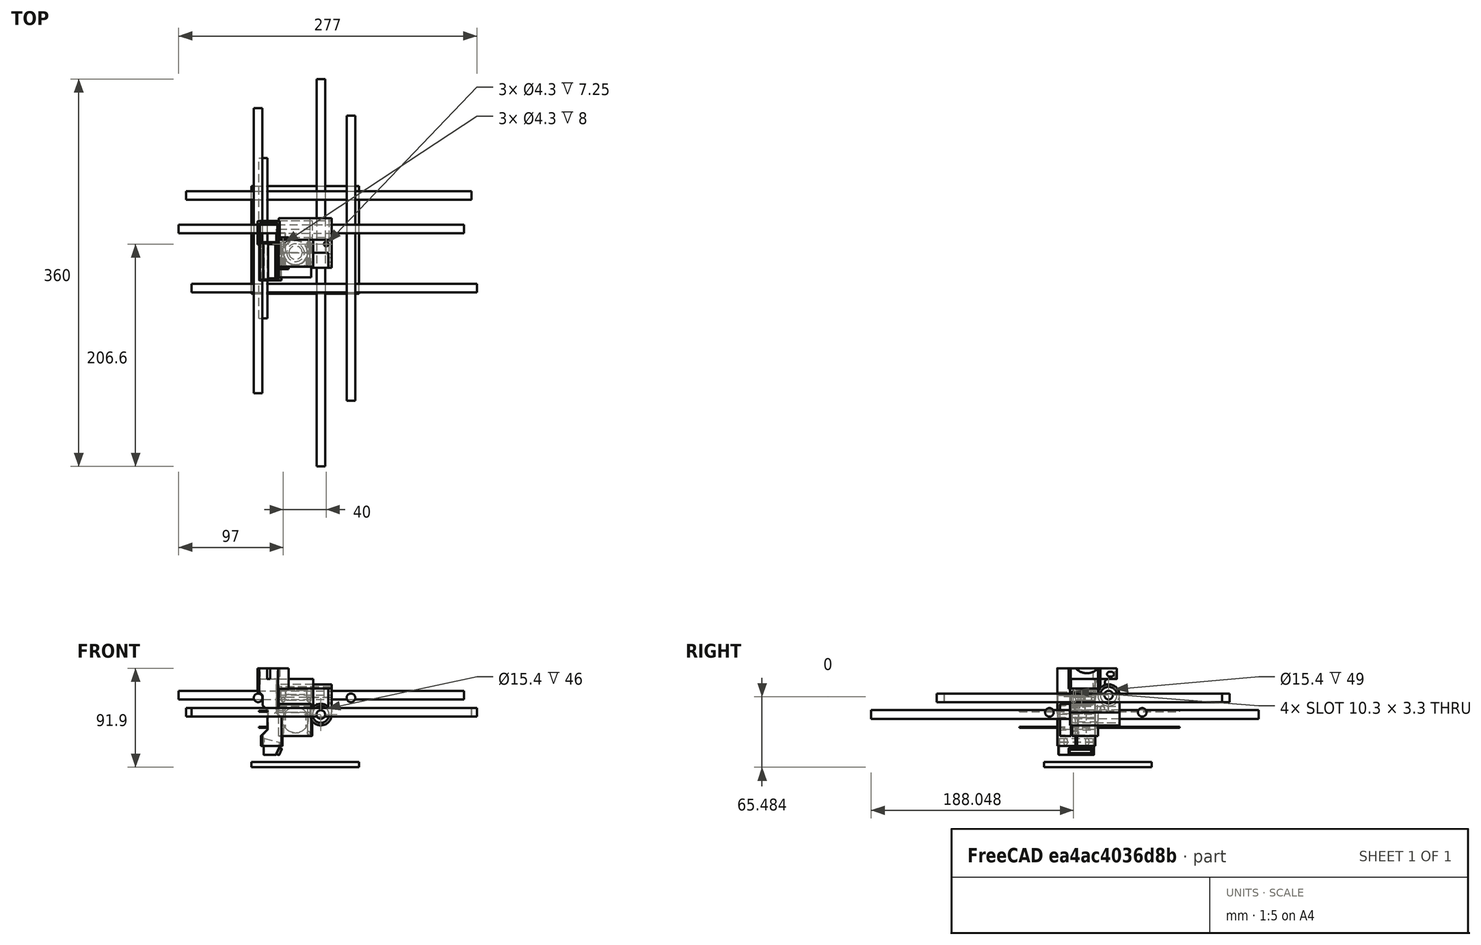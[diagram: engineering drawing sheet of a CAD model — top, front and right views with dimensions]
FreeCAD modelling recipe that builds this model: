
FCSTD DOCUMENT  (FreeCAD 0.17R)
Label: Carrier_E3DV6
License: All rights reserved
LicenseURL: http://en.wikipedia.org/wiki/All_rights_reserved
objects: Sketcher::SketchObject×28, App::DocumentObjectGroup×23, PartDesign::Pocket×21, PartDesign::FeatureBase×17, PartDesign::Body×7, PartDesign::Pad×6, Part::Box×6, Part::Cylinder×6, PartDesign::Fillet×5, Part::Feature×4, PartDesign::Line×3, Part::Cut×2, PartDesign::Revolution×1, App::Part×1, Mesh::Feature×1
note: 134 computed .brp shape members not serialized (recipe doc carries the construction recipe); baked Part::Feature solids carry a one-line shape summary decoded from their .brp

FEATURE [Sketcher::SketchObject] Sketch
  MapMode = 5
  Support = -> [XY_Plane]
  sketch-geometry (4):
    g0: LineSegment StartX=-15.5 StartY=12 StartZ=0 EndX=15.5 EndY=12 EndZ=0
    g1: LineSegment StartX=15.5 StartY=12 StartZ=0 EndX=15.5 EndY=-12 EndZ=0
    g2: LineSegment StartX=15.5 StartY=-12 StartZ=0 EndX=-15.5 EndY=-12 EndZ=0
    g3: LineSegment StartX=-15.5 StartY=-12 StartZ=0 EndX=-15.5 EndY=12 EndZ=0
  constraints (12):
    c: Coincident(g0,g1)
    c: Coincident(g1,g2)
    c: Coincident(g2,g3)
    c: Coincident(g3,g0)
    c: Horizontal(g0)
    c: Horizontal(g2)
    c: Vertical(g1)
    c: Vertical(g3)
    c: Symmetric(g0,g0,g-2)
    c: Symmetric(g0,g1,g-1)
    c: DistanceX(g0,g0) = 31
    c: DistanceY(g3,g3) = 24
FEATURE [PartDesign::Pad] Pad  label="FS_BaseBody"
  Length = 22
  Length2 = 100
  Profile = -> Sketch
  Type = 0
FEATURE [Sketcher::SketchObject] Sketch001
  ExternalGeometry = -> [Pad]
  MapMode = 5
  Placement = pos=(0,-12,0) rot=(1,0,0;1.5708rad)
  Support = -> [Pad]
  sketch-geometry (6):
    g0: LineSegment [constr] StartX=0 StartY=15 StartZ=0 EndX=-15.5 EndY=15 EndZ=0
    g1: Circle CenterX=0 CenterY=15 CenterZ=0 NormalX=0 NormalY=0 NormalZ=1 AngleXU=0 Radius=12
    g2: Circle CenterX=-12 CenterY=3 CenterZ=0 NormalX=0 NormalY=0 NormalZ=1 AngleXU=0 Radius=1.3
    g3: Circle CenterX=12 CenterY=3 CenterZ=0 NormalX=0 NormalY=0 NormalZ=1 AngleXU=0 Radius=1.3
    g4: Circle CenterX=12 CenterY=27 CenterZ=0 NormalX=0 NormalY=0 NormalZ=1 AngleXU=0 Radius=1.3
    g5: Circle CenterX=-12 CenterY=27 CenterZ=0 NormalX=0 NormalY=0 NormalZ=1 AngleXU=0 Radius=1.3
  constraints (16):
    c: PointOnObject(g0,g-2)
    c: PointOnObject(g0,g-3)
    c: Horizontal(g0)
    c: DistanceY(g-6,g0) = 15
    c: Coincident(g1,g0)
    c: Radius(g1) = 12
    c: Symmetric(g2,g3,g-2)
    c: Symmetric(g5,g4,g-2)
    c: Distance(g2,g3) = 24
    c: DistanceX(g5,g4) = 24
    c: Distance(g5,g2) = 24
    c: DistanceY(g-6,g2) = 3
    c: Radius(g5) = 1.3
    c: Equal(g5,g4)
    c: Equal(g5,g3)
    c: Equal(g5,g2)
FEATURE [PartDesign::Pocket] Pocket  label="FS_FanCutout_Pocket"
  BaseFeature = -> Pad
  Length = 6
  Length2 = 100
  Profile = -> Sketch001
  Type = 0
FEATURE [Sketcher::SketchObject] Sketch002
  MapMode = 5
  Placement = pos=(0,0,0) rot=(1,0,0;3.14159rad)
  Support = -> [Pocket]
  sketch-geometry (1):
    g0: Circle CenterX=0 CenterY=0 CenterZ=0 NormalX=0 NormalY=0 NormalZ=1 AngleXU=0 Radius=11.25
  constraints (3):
    c: PointOnObject(g0,g-1)
    c: Coincident(g0,g-1)
    c: Radius(g0) = 11.25
FEATURE [PartDesign::Pocket] Pocket001  label="FS_EDV6_Cutout_Pocket"
  BaseFeature = -> Pocket
  Length = 5
  Length2 = 100
  Profile = -> Sketch002
  Type = 1
FEATURE [Sketcher::SketchObject] Sketch003
  ExternalGeometry = -> [Pocket001]
  MapMode = 5
  Placement = pos=(0,12,0) rot=(0,0.707107,0.707107;3.14159rad)
  Support = -> [Pocket001]
  sketch-geometry (4):
    g0: LineSegment StartX=-11.25 StartY=22 StartZ=0 EndX=11.25 EndY=22 EndZ=0
    g1: LineSegment StartX=11.25 StartY=22 StartZ=0 EndX=11.25 EndY=0 EndZ=0
    g2: LineSegment StartX=11.25 StartY=0 StartZ=0 EndX=-11.25 EndY=0 EndZ=0
    g3: LineSegment StartX=-11.25 StartY=0 StartZ=0 EndX=-11.25 EndY=22 EndZ=0
  constraints (12):
    c: Coincident(g0,g1)
    c: Coincident(g1,g2)
    c: Coincident(g2,g3)
    c: Coincident(g3,g0)
    c: Horizontal(g0)
    c: Horizontal(g2)
    c: Vertical(g1)
    c: Vertical(g3)
    c: Symmetric(g1,g2,g-2)
    c: DistanceX(g0,g0) = 22.5
    c: PointOnObject(g2,g-1)
    c: PointOnObject(g0,g-3)
FEATURE [PartDesign::Pocket] Pocket002  label="FS_EDV6_Cutout_Back"
  BaseFeature = -> Pocket001
  Length = 11
  Length2 = 100
  Profile = -> Sketch003
  Type = 0
FEATURE [Sketcher::SketchObject] Sketch004
  ExternalGeometry = -> [Pocket002]
  MapMode = 5
  Placement = pos=(0,-12,0) rot=(1,0,0;1.5708rad)
  Support = -> [Pocket002]
  sketch-geometry (1):
    g0: Circle CenterX=23.47 CenterY=19.93 CenterZ=0 NormalX=0 NormalY=0 NormalZ=1 AngleXU=0 Radius=10.5
  constraints (3):
    c: Radius(g0) = 10.5
    c: DistanceY(g-1,g0) = 19.93
    c: DistanceX(g-1,g0) = 23.47
FEATURE [PartDesign::Pocket] Pocket003  label="FS_Cutout_Axis_Pocket"
  BaseFeature = -> Pocket002
  Length = 5
  Length2 = 100
  Profile = -> Sketch004
  Type = 1
FEATURE [Sketcher::SketchObject] Sketch005
  MapMode = 5
  Placement = pos=(0,0,0) rot=(1,0,0;1.5708rad)
  Support = -> [XZ_Plane001]
  sketch-geometry (4):
    g0: LineSegment StartX=-24.5 StartY=11 StartZ=0 EndX=24.5 EndY=11 EndZ=0
    g1: LineSegment StartX=24.5 StartY=11 StartZ=0 EndX=24.5 EndY=-11 EndZ=0
    g2: LineSegment StartX=24.5 StartY=-11 StartZ=0 EndX=-24.5 EndY=-11 EndZ=0
    g3: LineSegment StartX=-24.5 StartY=-11 StartZ=0 EndX=-24.5 EndY=11 EndZ=0
  constraints (12):
    c: Coincident(g0,g1)
    c: Coincident(g1,g2)
    c: Coincident(g2,g3)
    c: Coincident(g3,g0)
    c: Horizontal(g0)
    c: Horizontal(g2)
    c: Vertical(g1)
    c: Vertical(g3)
    c: DistanceX(g2,g2) = 49
    c: DistanceY(g1,g1) = 22
    c: Symmetric(g1,g2,g-2)
    c: Symmetric(g0,g1,g-1)
FEATURE [PartDesign::Pad] Pad001  label="HET1_Base_Pad"
  Length = 12
  Length2 = 100
  Placement = pos=(0,0,0) rot=(1,0,0;1.5708rad)
  Profile = -> Sketch005
  Type = 0
FEATURE [Sketcher::SketchObject] Sketch006  label="HET1_Holes_Top"
  ExternalGeometry = -> [Pad001]
  MapMode = 5
  Placement = pos=(0,-1e-12,11) rot=(0,0,1;3.14159rad)
  Support = -> [Pad001]
  sketch-geometry (4):
    g0: Circle CenterX=20.5 CenterY=4 CenterZ=0 NormalX=0 NormalY=0 NormalZ=1 AngleXU=0 Radius=2.15
    g1: Circle CenterX=-19.5 CenterY=4 CenterZ=0 NormalX=0 NormalY=0 NormalZ=1 AngleXU=0 Radius=2.15
    g2: LineSegment [constr] StartX=-19.5 StartY=4 StartZ=0 EndX=20.5 EndY=4 EndZ=0
    g3: Circle CenterX=-3.5 CenterY=4 CenterZ=0 NormalX=0 NormalY=0 NormalZ=1 AngleXU=0 Radius=2.15
  constraints (11):
    c: DistanceX(g1,g0) = 40
    c: Radius(g1) = 2.15
    c: Equal(g1,g0)
    c: DistanceX(g0,g-3) = 4
    c: DistanceY(g-3,g0) = 4
    c: Coincident(g2,g1)
    c: Coincident(g2,g0)
    c: Horizontal(g2)
    c: PointOnObject(g3,g2)
    c: Radius(g3) = 2.15
    c: DistanceX(g3,g0) = 24
FEATURE [PartDesign::Pocket] Pocket004  label="HET1_Holes_Top_Pocket"
  BaseFeature = -> Pad001
  Length = 8
  Length2 = 100
  Placement = pos=(0,0,0) rot=(1,0,0;1.5708rad)
  Profile = -> Sketch006
  Type = 0
FEATURE [Sketcher::SketchObject] Sketch007
  ExternalGeometry = -> [Pocket004]
  MapMode = 5
  Placement = pos=(0,-12,-1e-12) rot=(1,0,0;1.5708rad)
  Support = -> [Pocket004]
  sketch-geometry (2):
    g0: Circle CenterX=-20.5 CenterY=1 CenterZ=0 NormalX=0 NormalY=0 NormalZ=1 AngleXU=0 Radius=2.15
    g1: Circle CenterX=3.5 CenterY=1 CenterZ=0 NormalX=0 NormalY=0 NormalZ=1 AngleXU=0 Radius=2.15
  constraints (6):
    c: Radius(g0) = 2.15
    c: Equal(g0,g1)
    c: DistanceX(g0,g1) = 24
    c: DistanceX(g-3,g0) = 4
    c: DistanceY(g-3,g0) = 12
    c: DistanceY(g-3,g1) = 12
FEATURE [PartDesign::Pocket] Pocket005  label="HET1_Holes_Front_Pocket"
  BaseFeature = -> Pocket004
  Length = 6
  Length2 = 100
  Placement = pos=(0,0,0) rot=(1,0,0;1.5708rad)
  Profile = -> Sketch007
  Type = 0
FEATURE [Sketcher::SketchObject] Sketch008
  ExternalGeometry = -> [Pocket004]
  MapMode = 5
  Placement = pos=(0,0,-11) rot=(1,0,0;3.14159rad)
  Support = -> [Pocket005]
  sketch-geometry (6):
    g0: LineSegment StartX=-24.5 StartY=0 StartZ=0 EndX=-24.5 EndY=-9.75 EndZ=0
    g1: LineSegment StartX=-24.5 StartY=-9.75 StartZ=0 EndX=4.5 EndY=-9.75 EndZ=0
    g2: LineSegment StartX=4.5 StartY=-9.75 StartZ=0 EndX=4.5 EndY=-20 EndZ=0
    g3: LineSegment StartX=4.5 StartY=-20 StartZ=0 EndX=24.5 EndY=-20 EndZ=0
    g4: LineSegment StartX=24.5 StartY=-20 StartZ=0 EndX=24.5 EndY=0 EndZ=0
    g5: LineSegment StartX=24.5 StartY=0 StartZ=0 EndX=-24.5 EndY=0 EndZ=0
  constraints (16):
    c: Coincident(g0,g-3)
    c: Vertical(g0)
    c: Coincident(g0,g1)
    c: Horizontal(g1)
    c: Coincident(g1,g2)
    c: Coincident(g2,g3)
    c: Horizontal(g3)
    c: Coincident(g3,g4)
    c: Coincident(g4,g-4)
    c: Vertical(g4)
    c: Coincident(g4,g5)
    c: Coincident(g5,g0)
    c: DistanceY(g0,g0) = 9.75
    c: Vertical(g2)
    c: DistanceY(g4,g4) = 20
    c: DistanceX(g3,g3) = 20
FEATURE [PartDesign::Pad] Pad002  label="HET1_Support_Axis"
  BaseFeature = -> Pocket005
  Length = 14
  Length2 = 100
  Placement = pos=(0,0,0) rot=(1,0,0;1.5708rad)
  Profile = -> Sketch008
  Reversed = true
  Type = 0
FEATURE [Sketcher::SketchObject] Sketch009
  ExternalGeometry = -> [Pad002]
  MapMode = 5
  Placement = pos=(-24.5,0,0) rot=(0.707107,0,-0.707107;3.14159rad)
  Support = -> [Pad002]
  sketch-geometry (1):
    g0: Circle CenterX=7 CenterY=-4.25 CenterZ=0 NormalX=0 NormalY=0 NormalZ=1 AngleXU=0 Radius=2.15
  constraints (3):
    c: Radius(g0) = 2.15
    c: DistanceY(g0,g-1) = 4.25
    c: DistanceX(g-1,g0) = 7
FEATURE [PartDesign::Pocket] Pocket006  label="HET1_Mounthole_Fanduct1"
  BaseFeature = -> Pad002
  Length = 6
  Length2 = 100
  Placement = pos=(0,0,0) rot=(1,0,0;1.5708rad)
  Profile = -> Sketch009
  Type = 0
FEATURE [Sketcher::SketchObject] Sketch010
  ExternalGeometry = -> [Pocket006]
  MapMode = 5
  Placement = pos=(0,-12,-1e-12) rot=(1,0,0;1.5708rad)
  Support = -> [Pocket006]
  sketch-geometry (4):
    g0: LineSegment StartX=24.5 StartY=11 StartZ=0 EndX=21.5 EndY=11 EndZ=0
    g1: LineSegment StartX=21.5 StartY=11 StartZ=0 EndX=21.5 EndY=-11 EndZ=0
    g2: LineSegment StartX=21.5 StartY=-11 StartZ=0 EndX=24.5 EndY=-11 EndZ=0
    g3: LineSegment StartX=24.5 StartY=-11 StartZ=0 EndX=24.5 EndY=11 EndZ=0
  constraints (11):
    c: Coincident(g0,g1)
    c: Coincident(g1,g2)
    c: Coincident(g2,g3)
    c: Coincident(g3,g0)
    c: Horizontal(g0)
    c: Horizontal(g2)
    c: Vertical(g1)
    c: Vertical(g3)
    c: DistanceX(g2,g2) = 3
    c: Coincident(g0,g-3)
    c: Coincident(g2,g-3)
FEATURE [PartDesign::Pad] Pad003  label="HET1_MountingTab_Fanduct2"
  BaseFeature = -> Pocket006
  Length = 14
  Length2 = 100
  Placement = pos=(0,0,0) rot=(1,0,0;1.5708rad)
  Profile = -> Sketch010
  Type = 0
FEATURE [Sketcher::SketchObject] Sketch011
  ExternalGeometry = -> [Pad003]
  MapMode = 5
  Placement = pos=(24.5,0,0) rot=(0.707107,0,0.707107;3.14159rad)
  Support = -> [Pad003]
  sketch-geometry (8):
    g0: ArcOfCircle CenterX=6.98436 CenterY=22.5516 CenterZ=0 NormalX=0 NormalY=0 NormalZ=1 AngleXU=0 Radius=1.65 StartAngle=4.71239 EndAngle=7.85398
    g1: ArcOfCircle CenterX=-0.015642 CenterY=22.5516 CenterZ=0 NormalX=0 NormalY=0 NormalZ=1 AngleXU=0 Radius=1.65 StartAngle=1.5708 EndAngle=4.71239
    g2: LineSegment StartX=6.98436 StartY=24.2016 StartZ=0 EndX=-0.015642 EndY=24.2016 EndZ=0
    g3: LineSegment StartX=6.98436 StartY=20.9016 StartZ=0 EndX=-0.015642 EndY=20.9016 EndZ=0
    g4: ArcOfCircle CenterX=6.95398 CenterY=15.0516 CenterZ=0 NormalX=0 NormalY=0 NormalZ=1 AngleXU=0 Radius=1.65 StartAngle=4.71239 EndAngle=7.85398
    g5: ArcOfCircle CenterX=-0.0460183 CenterY=15.0516 CenterZ=0 NormalX=0 NormalY=0 NormalZ=1 AngleXU=0 Radius=1.65 StartAngle=1.5708 EndAngle=4.71239
    g6: LineSegment StartX=6.95398 StartY=16.7016 StartZ=0 EndX=-0.0460183 EndY=16.7016 EndZ=0
    g7: LineSegment StartX=6.95398 StartY=13.4016 StartZ=0 EndX=-0.0460183 EndY=13.4016 EndZ=0
  constraints (17):
    c: Tangent(g0,g3) = 1.5708
    c: Tangent(g0,g2) = -1.5708
    c: Tangent(g2,g1) = -1.5708
    c: Tangent(g3,g1) = 1.5708
    c: Horizontal(g2)
    c: Equal(g0,g1)
    c: Tangent(g4,g7) = 1.5708
    c: Tangent(g4,g6) = -1.5708
    c: Tangent(g6,g5) = -1.5708
    c: Tangent(g7,g5) = 1.5708
    c: Horizontal(g6)
    c: Equal(g4,g5)
    c: Radius(g4) = 1.65
    c: Equal(g4,g0)
    c: DistanceX(g5,g4) = 7
    c: DistanceX(g1,g0) = 7
    c: DistanceY(g5,g1) = 7.5
FEATURE [PartDesign::Pocket] Pocket007  label="HET1_MountingHoles_Fanduct2"
  BaseFeature = -> Pad003
  Length = 5
  Length2 = 100
  Placement = pos=(0,0,0) rot=(1,0,0;1.5708rad)
  Profile = -> Sketch011
  Type = 1
FEATURE [Sketcher::SketchObject] Sketch012
  ExternalGeometry = -> [Pocket007]
  MapMode = 5
  Placement = pos=(24.5,0,0) rot=(0.707107,0,0.707107;3.14159rad)
  Support = -> [Pocket007]
  sketch-geometry (1):
    g0: Circle CenterX=5 CenterY=-10 CenterZ=0 NormalX=0 NormalY=0 NormalZ=1 AngleXU=0 Radius=10
  constraints (3):
    c: DistanceY(g0,g-1) = 10
    c: DistanceX(g-1,g0) = 5
    c: Radius(g0) = 10
FEATURE [PartDesign::Pad] Pad004  label="HET1_X-Axis-Pad"
  BaseFeature = -> Pocket007
  Length = 10
  Length2 = 100
  Placement = pos=(0,0,0) rot=(1,0,0;1.5708rad)
  Profile = -> Sketch012
  Type = 3
  UpToFace = -> Pocket007 [Face2]
FEATURE [PartDesign::Line] DatumLine  label="Center_of_X-Axis_Datumline"
  AttacherType = Attacher::AttachEngineLine
  MapMode = 19
  Placement = pos=(24.5,9.93835,4.94442) rot=(0.535844,0.652489,0.535844;1.98535rad)
  Support = -> [Pad004]
FEATURE [Sketcher::SketchObject] Sketch013
  ExternalGeometry = -> [DatumLine]
  MapMode = 5
  Placement = pos=(0,20,0) rot=(-1,0,0;1.5708rad)
  Support = -> [Pad004]
  sketch-geometry (2):
    g0: Circle CenterX=14.5 CenterY=13.0556 CenterZ=0 NormalX=0 NormalY=0 NormalZ=1 AngleXU=0 Radius=10
    g1: LineSegment [constr] StartX=14.5 StartY=13.0556 StartZ=0 EndX=14.5 EndY=-4.94442 EndZ=0
  constraints (6):
    c: Radius(g0) = 10
    c: Coincident(g1,g0)
    c: PointOnObject(g1,g-3)
    c: Vertical(g1)
    c: Distance(g1) = 18
    c: DistanceX(g-1,g0) = 14.5
FEATURE [PartDesign::Pad] Pad005  label="HET1_Y-Axis-Pad"
  BaseFeature = -> Pad004
  Length = 46
  Length2 = 100
  Placement = pos=(0,0,0) rot=(1,0,0;1.5708rad)
  Profile = -> Sketch013
  Reversed = true
  Type = 0
FEATURE [Sketcher::SketchObject] Sketch014
  ExternalGeometry = -> [Pad005]
  MapMode = 5
  Placement = pos=(0,20,0) rot=(-1,0,0;1.5708rad)
  Support = -> [Pad005]
  sketch-geometry (1):
    g0: Circle CenterX=14.5 CenterY=13.0556 CenterZ=0 NormalX=0 NormalY=0 NormalZ=1 AngleXU=0 Radius=7.7
  constraints (1):
    c: Radius(g0) = 7.7
FEATURE [PartDesign::Pocket] Pocket008  label="HET1_Y-Axis-IGUS-Pocket"
  BaseFeature = -> Pad005
  Length = 5
  Length2 = 100
  Placement = pos=(0,0,0) rot=(1,0,0;1.5708rad)
  Profile = -> Sketch014
  Type = 1
FEATURE [Sketcher::SketchObject] Sketch015
  ExternalGeometry = -> [Pocket008]
  MapMode = 5
  Placement = pos=(24.5,0,0) rot=(0.707107,0,0.707107;3.14159rad)
  Support = -> [Pocket008]
  sketch-geometry (1):
    g0: Circle CenterX=5 CenterY=-10 CenterZ=0 NormalX=0 NormalY=0 NormalZ=1 AngleXU=0 Radius=7.7
  constraints (1):
    c: Radius(g0) = 7.7
FEATURE [PartDesign::Pocket] Pocket009  label="HET1_X-Axis-IGUS-Pocket"
  BaseFeature = -> Pocket008
  Length = 5
  Length2 = 100
  Placement = pos=(0,0,0) rot=(1,0,0;1.5708rad)
  Profile = -> Sketch015
  Type = 1
FEATURE [PartDesign::Line] DatumLine001  label="Center_of_Y-Axis_Datumline"
  AttacherType = Attacher::AttachEngineLine
  MapMode = 19
  Placement = pos=(24.5,10,5) rot=(-0.534522,0.654654,-0.534522;1.98231rad)
  Support = -> [Pocket009]
FEATURE [PartDesign::Body] Body001
  Group = -> [Sketch005,Pad001,Sketch006,Pocket004,Sketch007,Pocket005,Sketch008,Pad002,Sketch009,Pocket006,Sketch010,Pad003,Sketch011,Pocket007,Sketch012,Pad004,Sketch013,DatumLine,Pad005,Sketch014,Pocket008,Sketch015,Pocket009,DatumLine001]
  Origin = -> Origin001
  Tip = -> Pocket009
FEATURE [App::DocumentObjectGroup] Group005  label="HET1_BaseBody"
  Group = -> [Body001]
FEATURE [Sketcher::SketchObject] Sketch064  label="E3DV6_Negative_Form_MitSpiel002"
  MapMode = 5
  Placement = pos=(0,0,0) rot=(1,0,0;1.5708rad)
  Support = -> [XZ_Plane002]
  sketch-geometry (15):
    g0: LineSegment StartX=0 StartY=0 StartZ=0 EndX=11.4 EndY=0 EndZ=0
    g1: LineSegment StartX=11.4 StartY=0 StartZ=0 EndX=11.4 EndY=26 EndZ=0
    g2: LineSegment StartX=8.2 StartY=33.2 StartZ=0 EndX=6.2 EndY=33.2 EndZ=0
    g3: LineSegment StartX=6.2 StartY=33.2 StartZ=0 EndX=6.2 EndY=38.8 EndZ=0
    g4: LineSegment StartX=6.2 StartY=38.8 StartZ=0 EndX=8.2 EndY=38.8 EndZ=0
    g5: LineSegment StartX=8.2 StartY=38.8 StartZ=0 EndX=8.2 EndY=42.7 EndZ=0
    g6: LineSegment StartX=8.2 StartY=33.2 StartZ=0 EndX=8.2 EndY=29.9 EndZ=0
    g7: LineSegment StartX=8.2 StartY=29.9 StartZ=0 EndX=6.2 EndY=29.9 EndZ=0
    g8: LineSegment StartX=6.2 StartY=29.9 StartZ=0 EndX=6.2 EndY=28.8 EndZ=0
    g9: LineSegment StartX=6.2 StartY=28.8 StartZ=0 EndX=11.4 EndY=28.8 EndZ=0
    g10: LineSegment StartX=11.4 StartY=28.8 StartZ=0 EndX=11.4 EndY=26 EndZ=0
    g11: LineSegment StartX=0 StartY=44.2 StartZ=0 EndX=0 EndY=0 EndZ=0
    g12: LineSegment StartX=8.2 StartY=42.7 StartZ=0 EndX=11 EndY=42.7 EndZ=0
    g13: LineSegment StartX=11 StartY=42.7 StartZ=0 EndX=11 EndY=44.2 EndZ=0
    g14: LineSegment StartX=11 StartY=44.2 StartZ=0 EndX=0 EndY=44.2 EndZ=0
  constraints (45):
    c: Coincident(g-1,g0)
    c: Horizontal(g0)
    c: Coincident(g0,g1)
    c: Vertical(g1)
    c: Coincident(g2,g3)
    c: Vertical(g3)
    c: Coincident(g3,g4)
    c: Horizontal(g4)
    c: Coincident(g4,g5)
    c: PointOnObject(g11,g-2)
    c: Vertical(g5)
    c: Horizontal(g2)
    c: DistanceX(g0,g0) = 11.4
    c: DistanceY(g1,g1) = 26
    c: DistanceY(g-1,g5) = 42.7
    c: DistanceY(g5,g5) = 3.9
    c: DistanceX(g11,g3) = 6.2
    c: DistanceY(g3,g3) = 5.6
    c: DistanceX(g11,g5) = 8.2
    c: DistanceX(g11,g2) = 8.2
    c: Vertical(g6)
    c: DistanceY(g6,g6) = 3.3
    c: Horizontal(g7)
    c: Coincident(g7,g8)
    c: Vertical(g8)
    c: Coincident(g8,g9)
    c: Horizontal(g9)
    c: Coincident(g6,g2)
    c: Coincident(g6,g7)
    c: DistanceY(g8,g8) = 1.1
    c: DistanceX(g11,g7) = 6.2
    c: Coincident(g10,g9)
    c: Coincident(g10,g1)
    c: Vertical(g10)
    c: Vertical(g11)
    c: Coincident(g11,g-1)
    c: Coincident(g5,g12)
    c: Horizontal(g12)
    c: Coincident(g12,g13)
    c: Vertical(g13)
    c: Coincident(g13,g14)
    c: Horizontal(g14)
    c: Coincident(g11,g14)
    c: Distance(g14) = 11
    c: DistanceY(g13,g13) = 1.5
FEATURE [PartDesign::Revolution] Revolution  label="E3DV6_Negative_Form_MitSpiel"
  Angle = 360
  Axis = (0,0,1)
  Base = (0,0,0)
  Placement = pos=(0,0,0) rot=(1,0,0;1.5708rad)
  Profile = -> Sketch064
  ReferenceAxis = -> Sketch064 [V_Axis]
  Reversed = true
FEATURE [PartDesign::Body] Body002  label="E3DV6_Negative_Form_Enlarged_Body_wpiezospace"
  Group = -> [Sketch064,Revolution]
  Origin = -> Origin002
  Placement = pos=(-9,-12,-33) rot=(0,0,1;0rad)
  Tip = -> Revolution
FEATURE [App::DocumentObjectGroup] Group003  label="Supports"
  Group = -> [Body002]
FEATURE [PartDesign::FeatureBase] Clone  label="HET1_BaseBody_Clone"
  Placement = pos=(0,0,0) rot=(1,0,0;1.5708rad)
FEATURE [PartDesign::FeatureBase] Clone001  label="E3DV6_Clone"
  Placement = pos=(-9,-12,-33) rot=(0,0,1;0rad)
FEATURE [PartDesign::Body] CloneBody
  Group = -> [Clone]
  Origin = -> Origin005
  Tip = -> Clone
FEATURE [PartDesign::Body] Clone001Body
  Group = -> [Clone001]
  Origin = -> Origin006
  Tip = -> Clone001
FEATURE [Part::Cut] Cut  label="HET1_TheCut"
  Base = -> CloneBody
  Tool = -> Clone001Body
FEATURE [PartDesign::FeatureBase] BaseFeature  label="HET1_TheCut_Basefeature"
  BaseFeature = -> Cut
FEATURE [App::Part] Part
  Group = -> [CloneBody,Clone001Body]
  License = CC BY 3.0
  LicenseURL = http://creativecommons.org/licenses/by/3.0/
  Origin = -> Origin004
FEATURE [PartDesign::Fillet] Fillet
  Base = -> BaseFeature [Edge172,Edge177,Edge162,Edge182,Edge8,Edge9,Edge10,Edge126,Edge52,Edge36]
  BaseFeature = -> BaseFeature
  Radius = 0.75
FEATURE [PartDesign::Fillet] Fillet001
  Base = -> Fillet [Edge49,Edge51,Edge47,Edge45,Edge28,Edge30,Edge32,Edge34,Edge110,Edge108,Edge111,Edge115,Edge114]
  BaseFeature = -> Fillet
  Radius = 0.5
FEATURE [PartDesign::Body] Body003  label="HET1_FilletsAndStuff"
  BaseFeature = -> Cut
  Group = -> [BaseFeature,Fillet,Fillet001]
  Origin = -> Origin003
  Tip = -> Fillet001
FEATURE [App::DocumentObjectGroup] Group006  label="HET1_FinalPart"
  Group = -> [Cut,Body003,Part]
FEATURE [Part::Box] Box009  label="EDDMount_Teil004"
  AttacherType = Attacher::AttachEngine3D
  Height = 22
  Length = 32
  Placement = pos=(-24.5,-25,-11) rot=(0,0,1;0rad)
  Width = 13
FEATURE [Sketcher::SketchObject] Sketch066
  MapMode = 5
  Placement = pos=(-24.5,-25,-11) rot=(1,0,0;1.5708rad)
  Support = -> [Box009]
  sketch-geometry (3):
    g0: Circle CenterX=15.5761 CenterY=-7.03196 CenterZ=0 NormalX=0 NormalY=0 NormalZ=1 AngleXU=0 Radius=12
    g1: Circle CenterX=3.49904 CenterY=4.96686 CenterZ=0 NormalX=0 NormalY=0 NormalZ=1 AngleXU=0 Radius=1.3
    g2: Circle CenterX=27.479 CenterY=5.01116 CenterZ=0 NormalX=0 NormalY=0 NormalZ=1 AngleXU=0 Radius=1.3
  constraints (3):
    c: Radius(g0) = 12
    c: Radius(g2) = 1.3
    c: Equal(g2,g1)
FEATURE [PartDesign::Pocket] Pocket042006  label="HET2_Löcher_Fan001"
  Length = 8
  Length2 = 100
  Placement = pos=(-24.5,-25,-11) rot=(0,0,1;0rad)
  Profile = -> Sketch066
  Type = 0
FEATURE [Sketcher::SketchObject] Sketch067
  ExternalGeometry = -> [Pocket042006]
  MapMode = 5
  Placement = pos=(-24.5,-25,11) rot=(0,0,1;0rad)
  Support = -> [Pocket042006]
  sketch-geometry (2):
    g0: Circle CenterX=4 CenterY=4 CenterZ=0 NormalX=0 NormalY=0 NormalZ=1 AngleXU=0 Radius=2.15
    g1: Circle CenterX=28 CenterY=4 CenterZ=0 NormalX=0 NormalY=0 NormalZ=1 AngleXU=0 Radius=2.15
  constraints (6):
    c: Radius(g1) = 2.15
    c: Equal(g1,g0)
    c: DistanceY(g-1,g0) = 4
    c: DistanceX(g-1,g0) = 4
    c: DistanceX(g0,g1) = 24
    c: DistanceY(g-1,g1) = 4
FEATURE [PartDesign::Pocket] Pocket042007  label="HET2_Befestigungslöcher_Clamp001"
  Length = 8
  Length2 = 100
  Placement = pos=(-24.5,-25,-11) rot=(0,0,1;0rad)
  Profile = -> Sketch067
  Type = 0
FEATURE [Sketcher::SketchObject] Sketch068
  ExternalGeometry = -> [Pocket042007]
  MapMode = 5
  Placement = pos=(-24.5,-25,-11) rot=(1,0,0;1.5708rad)
  Support = -> [Pocket042007]
  sketch-geometry (3):
    g0: LineSegment [constr] StartX=0 StartY=12 StartZ=0 EndX=32 EndY=12 EndZ=0
    g1: Circle CenterX=4 CenterY=12 CenterZ=0 NormalX=0 NormalY=0 NormalZ=1 AngleXU=0 Radius=1.6
    g2: Circle CenterX=28 CenterY=12 CenterZ=0 NormalX=0 NormalY=0 NormalZ=1 AngleXU=0 Radius=1.6
  constraints (10):
    c: PointOnObject(g0,g-3)
    c: Horizontal(g0)
    c: PointOnObject(g0,g-4)
    c: PointOnObject(g1,g0)
    c: PointOnObject(g2,g0)
    c: Radius(g2) = 1.6
    c: Equal(g2,g1)
    c: DistanceX(g-1,g1) = 4
    c: DistanceX(g1,g2) = 24
    c: DistanceY(g-1,g0) = 12
FEATURE [PartDesign::Pocket] Pocket042008  label="HET2_Besfestigungslöcher_HET002"
  Length = 5
  Length2 = 100
  Placement = pos=(-24.5,-25,-11) rot=(0,0,1;0rad)
  Profile = -> Sketch068
  Type = 1
FEATURE [Sketcher::SketchObject] Sketch069
  MapMode = 5
  Placement = pos=(-24.5,-25,-11) rot=(1,0,0;1.5708rad)
  Support = -> [Pocket042008]
  sketch-geometry (1):
    g0: Circle CenterX=38.9887 CenterY=-2.09718 CenterZ=0 NormalX=0 NormalY=0 NormalZ=1 AngleXU=0 Radius=10.5
  constraints (1):
    c: Radius(g0) = 10.5
FEATURE [PartDesign::Pocket] Pocket042009  label="HET2_Fertiger_Grundkörper001"
  Length = 5
  Length2 = 100
  Placement = pos=(-24.5,-25,-11) rot=(0,0,1;0rad)
  Profile = -> Sketch069
  Type = 1
FEATURE [PartDesign::FeatureBase] Clone002
  BaseFeature = -> Body002
  Placement = pos=(-9,-12,-33) rot=(0,0,1;0rad)
FEATURE [Part::Cut] Cut001
  Base = -> Pocket042008
  Tool = -> Clone002
FEATURE [App::DocumentObjectGroup] Group025  label="Zwischenschritte001"
  Group = -> [Box009,Pocket042006,Pocket042007,Cut001]
FEATURE [App::DocumentObjectGroup] Group024  label="HET2_HotEndBlock2"
  Group = -> [Group025]
FEATURE [PartDesign::FeatureBase] BaseFeature001
  BaseFeature = -> Cut001
FEATURE [PartDesign::Fillet] Fillet002  label="HET2_Fillets"
  Base = -> BaseFeature001 [Edge25,Edge23,Edge27,Edge29,Edge31,Edge51,Edge54,Edge56,Edge58,Edge60,Edge63,Edge20,Edge78,Edge76,Edge75,Edge72,Edge71,Edge13,Edge12,Edge11,Edge10,Edge4,Edge2,Edge41,Edge17,Edge19,Edge18]
  BaseFeature = -> BaseFeature001
  Radius = 0.5
FEATURE [PartDesign::Line] DatumLine002
  AttacherType = Attacher::AttachEngineLine
  MapMode = 19
  Placement = pos=(14.5,-26,-13.0556) rot=(-1,0,0;1.5708rad)
  Support = -> [Cut]
FEATURE [Sketcher::SketchObject] Sketch070
  ExternalGeometry = -> [DatumLine002]
  MapMode = 5
  Placement = pos=(0,-25,0) rot=(1,0,0;1.5708rad)
  Support = -> [Fillet002]
  sketch-geometry (1):
    g0: Circle CenterX=14.5 CenterY=-13.0556 CenterZ=0 NormalX=0 NormalY=0 NormalZ=1 AngleXU=0 Radius=10.5
  constraints (2):
    c: Coincident(g0,g-3)
    c: Radius(g0) = 10.5
FEATURE [PartDesign::Pocket] Pocket042010  label="HET2_Final_Pocket"
  BaseFeature = -> Fillet002
  Length = 5
  Length2 = 100
  Profile = -> Sketch070
  Type = 1
FEATURE [PartDesign::Body] Body004  label="HET2_Final_Body"
  BaseFeature = -> Cut001
  Group = -> [BaseFeature001,Fillet002,DatumLine002,Sketch070,Pocket042010]
  Origin = -> Origin007
  Tip = -> Pocket042010
FEATURE [App::DocumentObjectGroup] Group026  label="HET2"
  Group = -> [Group024,Pocket042009,Body004]
FEATURE [PartDesign::FeatureBase] Clone003  label="A_HET2"
  BaseFeature = -> Pocket042010
FEATURE [PartDesign::FeatureBase] Clone004  label="A_HET1"
  BaseFeature = -> Fillet001
FEATURE [Part::Box] Box004  label="Clamp_Cube"
  AttacherType = Attacher::AttachEngine3D
  Height = 9
  Length = 32
  Placement = pos=(-24.5,-25,11) rot=(0,0,1;0rad)
  Width = 25
FEATURE [Sketcher::SketchObject] Sketch074
  MapMode = 5
  Placement = pos=(-24.5,-25,11) rot=(1,0,0;3.14159rad)
  Support = -> [Box004]
  sketch-geometry (1):
    g0: Circle CenterX=15.5175 CenterY=-12.4529 CenterZ=0 NormalX=0 NormalY=0 NormalZ=1 AngleXU=0 Radius=4.25
  constraints (1):
    c: Radius(g0) = 4.25
FEATURE [PartDesign::Pocket] Pocket010  label="Clamp_Hotendloch_Mitte"
  Length = 5
  Length2 = 100
  Placement = pos=(-24.5,-25,11) rot=(0,0,1;0rad)
  Profile = -> Sketch074
  Type = 1
FEATURE [Sketcher::SketchObject] Sketch073
  ExternalGeometry = -> [Pocket010]
  MapMode = 5
  Placement = pos=(-24.5,-25,11) rot=(1,0,0;3.14159rad)
  Support = -> [Pocket010]
  sketch-geometry (1):
    g0: Circle CenterX=15.5175 CenterY=-12.4529 CenterZ=0 NormalX=0 NormalY=0 NormalZ=1 AngleXU=0 Radius=9
  constraints (2):
    c: Coincident(g0,g-3)
    c: Radius(g0) = 9
FEATURE [PartDesign::Pocket] Pocket011  label="Clamp_Piezoausparrung"
  Length = 1
  Length2 = 100
  Placement = pos=(-24.5,-25,11) rot=(0,0,1;0rad)
  Profile = -> Sketch073
  Type = 0
FEATURE [Sketcher::SketchObject] Sketch072
  ExternalGeometry = -> [Pocket011]
  MapMode = 5
  Placement = pos=(-24.5,-25,12) rot=(1,0,0;3.14159rad)
  Support = -> [Pocket011]
  sketch-geometry (7):
    g0: LineSegment StartX=22.2175 StartY=-16.3212 StartZ=0 EndX=22.2175 EndY=-8.58466 EndZ=0
    g1: LineSegment StartX=22.2175 StartY=-8.58466 StartZ=0 EndX=15.5175 EndY=-4.71641 EndZ=0
    g2: LineSegment StartX=15.5175 StartY=-4.71641 StartZ=0 EndX=8.81755 EndY=-8.58466 EndZ=0
    g3: LineSegment StartX=8.81755 StartY=-8.58466 StartZ=0 EndX=8.81755 EndY=-16.3212 EndZ=0
    g4: LineSegment StartX=8.81755 StartY=-16.3212 StartZ=0 EndX=15.5175 EndY=-20.1894 EndZ=0
    g5: LineSegment StartX=15.5175 StartY=-20.1894 StartZ=0 EndX=22.2175 EndY=-16.3212 EndZ=0
    g6: Circle [constr] CenterX=15.5175 CenterY=-12.4529 CenterZ=0 NormalX=0 NormalY=0 NormalZ=1 AngleXU=0 Radius=7.73649
  constraints (16):
    c: Coincident(g0,g1)
    c: Coincident(g1,g2)
    c: Coincident(g2,g3)
    c: Coincident(g3,g4)
    c: Coincident(g4,g5)
    c: Coincident(g5,g0)
    c: Equal(g0, g1-g5) x5
    c: PointOnObject(g0,g6)
    c: PointOnObject(g1,g6)
    c: PointOnObject(g2,g6)
    c: PointOnObject(g3,g6)
    c: PointOnObject(g4,g6)
    c: PointOnObject(g5,g6)
    c: Coincident(g6,g-3)
    c: Vertical(g0)
    c: DistanceX(g2,g0) = 13.4
FEATURE [PartDesign::Pocket] Pocket012  label="Clamp_M8_Mutter"
  Length = 7
  Length2 = 100
  Placement = pos=(-24.5,-25,11) rot=(0,0,1;0rad)
  Profile = -> Sketch072
  Type = 0
FEATURE [Sketcher::SketchObject] Sketch071
  MapMode = 5
  Placement = pos=(-24.5,-25,11) rot=(1,0,0;3.14159rad)
  Support = -> [Pocket012]
  sketch-geometry (4):
    g0: LineSegment StartX=13.1906 StartY=0 StartZ=0 EndX=17.1906 EndY=0 EndZ=0
    g1: LineSegment StartX=17.1906 StartY=0 StartZ=0 EndX=17.1906 EndY=-6.45807 EndZ=0
    g2: LineSegment StartX=17.1906 StartY=-6.45807 StartZ=0 EndX=13.1906 EndY=-6.45807 EndZ=0
    g3: LineSegment StartX=13.1906 StartY=-6.45807 StartZ=0 EndX=13.1906 EndY=0 EndZ=0
  constraints (10):
    c: Coincident(g0,g1)
    c: Coincident(g1,g2)
    c: Coincident(g2,g3)
    c: Coincident(g3,g0)
    c: Horizontal(g0)
    c: Horizontal(g2)
    c: Vertical(g1)
    c: Vertical(g3)
    c: PointOnObject(g0,g-1)
    c: DistanceX(g2,g2) = 4
FEATURE [PartDesign::Pocket] Pocket013  label="Clamp_Kabelauslass"
  Length = 2.5
  Length2 = 100
  Placement = pos=(-24.5,-25,11) rot=(0,0,1;0rad)
  Profile = -> Sketch071
  Type = 0
FEATURE [Sketcher::SketchObject] Sketch027
  ExternalGeometry = -> [Pocket013]
  MapMode = 5
  Placement = pos=(-24.5,-25,20) rot=(0,0,1;0rad)
  Support = -> [Pocket013]
  sketch-geometry (5):
    g0: Circle CenterX=4 CenterY=4 CenterZ=0 NormalX=0 NormalY=0 NormalZ=1 AngleXU=0 Radius=1.7
    g1: Circle CenterX=4 CenterY=21 CenterZ=0 NormalX=0 NormalY=0 NormalZ=1 AngleXU=0 Radius=1.7
    g2: Circle CenterX=44 CenterY=21 CenterZ=0 NormalX=0 NormalY=0 NormalZ=1 AngleXU=0 Radius=1.7
    g3: Circle CenterX=28 CenterY=4 CenterZ=0 NormalX=0 NormalY=0 NormalZ=1 AngleXU=0 Radius=1.7
    g4: Circle CenterX=28 CenterY=21 CenterZ=0 NormalX=0 NormalY=0 NormalZ=1 AngleXU=0 Radius=1.7
  constraints (15):
    c: Radius(g0) = 1.7
    c: Equal(g0,g1)
    c: Equal(g0,g3)
    c: Equal(g0,g2)
    c: DistanceX(g0,g3) = 24
    c: DistanceY(g-1,g0) = 4
    c: DistanceY(g-1,g3) = 4
    c: DistanceY(g1,g-3) = 4
    c: DistanceX(g-3,g1) = 4
    c: DistanceX(g1,g2) = 40
    c: DistanceY(g2,g-3) = 4
    c: DistanceX(g-1,g0) = 4
    c: DistanceX(g-3,g4) = 28
    c: DistanceY(g4,g-3) = 4
    c: Equal(g4,g3)
FEATURE [PartDesign::Pocket] Pocket026  label="Clamp_Befestigungslöcher_HETx"
  Length = 5
  Length2 = 100
  Placement = pos=(-24.5,-25,11) rot=(0,0,1;0rad)
  Profile = -> Sketch027
  Type = 1
FEATURE [PartDesign::Fillet] Fillet016  label="Clamp_Final"
  Base = -> Pocket026 [Edge1,Edge3,Edge20,Edge10,Edge15,Edge17,Edge14,Edge18]
  Placement = pos=(-22,-35,6) rot=(0,0,1;0rad)
  Radius = 1
FEATURE [App::DocumentObjectGroup] Group027  label="Clamp"
  Group = -> [Box004,Pocket010,Pocket011,Pocket012,Pocket013,Pocket026,Fillet016]
FEATURE [PartDesign::FeatureBase] Clone006  label="A_Clamp"
  BaseFeature = -> Fillet016
  Placement = pos=(-24.5,-25,11) rot=(0,0,1;0rad)
FEATURE [App::DocumentObjectGroup] Group029  label="HET1"
  Group = -> [Group005,Group006]
FEATURE [App::DocumentObjectGroup] Group033  label="read_readme.md for license of this folder"
FEATURE [PartDesign::Fillet] Fillet017  label="FS_Final_Fillets"
  Base = -> Pocket003 [Edge30,Edge29,Edge5,Edge21,Edge7,Edge9,Edge14]
  BaseFeature = -> Pocket003
  Radius = 0.5
FEATURE [PartDesign::Body] Body  label="FanShroud_Body"
  Group = -> [Sketch,Pad,Sketch001,Pocket,Sketch002,Pocket001,Sketch003,Pocket002,Sketch004,Pocket003,Fillet017]
  Origin = -> Origin
  Placement = pos=(-9,-12,-33) rot=(0,0,1;0rad)
  Tip = -> Fillet017
FEATURE [App::DocumentObjectGroup] Group004  label="FanShroud"
  Group = -> [Body]
FEATURE [App::DocumentObjectGroup] Group  label="Development"
  Group = -> [Group029,Group026,Group027,Group004]
FEATURE [PartDesign::FeatureBase] Clone007  label="A_FanShroud"
  BaseFeature = -> Fillet017
  Placement = pos=(-9,-13,-33) rot=(0,0,1;0rad)
FEATURE [Part::Box] Box007  label="Glasssimulation"
  AttacherType = Attacher::AttachEngine3D
  Height = 5
  Length = 100
  Placement = pos=(-50,-50,-62) rot=(0,0,1;0rad)
  Width = 100
FEATURE [Part::Feature] E3D_V6_1_75mm_Universal_HotEnd_Mockup001001  label="E3D_V6_1_75mm_Universal_HotEnd_Mockup002"
  shape: bbox 22.3 x 26.65 x 62.3 mm, 3720 faces, 0 solids (baked)
FEATURE [App::DocumentObjectGroup] Group034  label="E3DV6-Model_CC-BY-3.0"
  Group = -> [E3D_V6_1_75mm_Universal_HotEnd_Mockup001001]
FEATURE [PartDesign::FeatureBase] Clone008  label="E3D_V6_1_75mm_Universal_HotEnd_Mockup003"
  BaseFeature = -> E3D_V6_1_75mm_Universal_HotEnd_Mockup001001
FEATURE [Part::Feature] LM8UU_by_3drap_dia8_1001_solid001001  label="LM8UU_by_3drap_dia8_1"
  Placement = pos=(0,0,0) rot=(0,1,0;1.5708rad)
  shape: bbox 24 x 15 x 15 mm, 5662 faces (baked)
FEATURE [App::DocumentObjectGroup] Group035  label="LM8UU"
  Group = -> [LM8UU_by_3drap_dia8_1001_solid001001]
FEATURE [App::DocumentObjectGroup] Group031  label="3rdPartyModels"
  Group = -> [Group033,Group034,Group035]
FEATURE [PartDesign::FeatureBase] Clone009  label="LM8UU_by_3drap_dia8_1_Clone"
  BaseFeature = -> LM8UU_by_3drap_dia8_1001_solid001001
  Placement = pos=(0,2.5,12.5) rot=(0,1,0;1.5708rad)
FEATURE [PartDesign::FeatureBase] Clone010  label="LM8UU_by_3drap_dia8_1_Clone2"
  BaseFeature = -> LM8UU_by_3drap_dia8_1001_solid001001
  Placement = pos=(-24,2.5,12.5) rot=(0,1,0;1.5708rad)
FEATURE [PartDesign::FeatureBase] Clone011  label="LM8UU_by_3drap_dia8_1_Clone3"
  BaseFeature = -> LM8UU_by_3drap_dia8_1001_solid001001
  Placement = pos=(22,-3,-5.5) rot=(0.57735,-0.57735,-0.57735;4.18879rad)
FEATURE [PartDesign::FeatureBase] Clone012  label="LM8UU_by_3drap_dia8_1_Clone4"
  BaseFeature = -> LM8UU_by_3drap_dia8_1001_solid001001
  Placement = pos=(22,-27,-5.5) rot=(0.57735,-0.57735,-0.57735;4.18879rad)
FEATURE [Part::Box] Box001  label="FAN 30x30x10"
  AttacherType = Attacher::AttachEngine3D
  Height = 10
  Length = 30
  Placement = pos=(-24.5,-25,-33) rot=(1,0,0;1.5708rad)
  Width = 30
FEATURE [Sketcher::SketchObject] Sketch075
  ExternalGeometry = -> [Box001]
  MapMode = 5
  Placement = pos=(-24.5,-35,-33) rot=(1,0,0;1.5708rad)
  Support = -> [Box001]
  sketch-geometry (5):
    g0: Circle CenterX=15 CenterY=15 CenterZ=0 NormalX=0 NormalY=0 NormalZ=1 AngleXU=0 Radius=12.4141
    g1: Circle CenterX=3 CenterY=27 CenterZ=0 NormalX=0 NormalY=0 NormalZ=1 AngleXU=0 Radius=1.75
    g2: Circle CenterX=27 CenterY=27 CenterZ=0 NormalX=0 NormalY=0 NormalZ=1 AngleXU=0 Radius=1.75
    g3: Circle CenterX=27 CenterY=3 CenterZ=0 NormalX=0 NormalY=0 NormalZ=1 AngleXU=0 Radius=1.75
    g4: Circle CenterX=3 CenterY=3 CenterZ=0 NormalX=0 NormalY=0 NormalZ=1 AngleXU=0 Radius=1.75
  constraints (14):
    c: Radius(g1) = 1.75
    c: Equal(g1,g2)
    c: Equal(g1,g3)
    c: Equal(g1,g4)
    c: DistanceX(g1,g2) = 24
    c: DistanceX(g4,g3) = 24
    c: DistanceY(g4,g1) = 24
    c: DistanceX(g-1,g0) = 15
    c: DistanceY(g-1,g0) = 15
    c: DistanceY(g-1,g4) = 3
    c: DistanceY(g-4,g3) = 3
    c: DistanceX(g-5,g1) = 3
    c: DistanceY(g3,g2) = 24
    c: DistanceX(g3,g-4) = 3
FEATURE [PartDesign::Pocket] Pocket042011
  Length = 5
  Length2 = 100
  Placement = pos=(-24.5,-25,-33) rot=(1,0,0;1.5708rad)
  Profile = -> Sketch075
  Type = 1
FEATURE [App::DocumentObjectGroup] Group028  label="Fan"
  Group = -> [Box001,Pocket042011]
FEATURE [Part::Cylinder] Cylinder001  label="Y-Achse"
  Angle = 360
  AttacherType = Attacher::AttachEngine3D
  Height = 265
  Placement = pos=(-117.5,10,5) rot=(0.57735,0.57735,0.57735;2.0944rad)
  Radius = 4
FEATURE [Part::Cylinder] Cylinder  label="X-Achse"
  Angle = 360
  AttacherType = Attacher::AttachEngine3D
  Height = 360
  Placement = pos=(14.5,149.4,-13) rot=(1,0,0;1.5708rad)
  Radius = 4
FEATURE [App::DocumentObjectGroup] Group037  label="Axis-through-hotend"
  Group = -> [Cylinder,Cylinder001]
FEATURE [Part::Cylinder] Cylinder008  label="Y-Achse002"
  Angle = 360
  AttacherType = Attacher::AttachEngine3D
  Height = 265
  Placement = pos=(-105.5,-45,-11) rot=(0.57735,0.57735,0.57735;2.0944rad)
  Radius = 4
FEATURE [Part::Cylinder] Cylinder010  label="Y-Achse003"
  Angle = 360
  AttacherType = Attacher::AttachEngine3D
  Height = 265
  Placement = pos=(-110.5,41.25,-11) rot=(0.57735,0.57735,0.57735;2.0944rad)
  Radius = 4
FEATURE [App::DocumentObjectGroup] Group038  label="Y"
  Group = -> [Cylinder010,Cylinder008]
FEATURE [Part::Box] Box  label="Belt1"
  AttacherType = Attacher::AttachEngine3D
  Height = 1
  Length = 8
  Placement = pos=(-43,-73,-10.5) rot=(0,0,1;0rad)
  Width = 149
FEATURE [Part::Box] Box011  label="Belt002"
  AttacherType = Attacher::AttachEngine3D
  Height = 1
  Length = 8
  Placement = pos=(-43,-73,-25.5) rot=(0,0,1;0rad)
  Width = 149
FEATURE [Part::Cylinder] Cylinder012  label="X-Achse004"
  Angle = 360
  AttacherType = Attacher::AttachEngine3D
  Height = 265
  Placement = pos=(-43.75,122.4,2.5) rot=(1,0,0;1.5708rad)
  Radius = 4
FEATURE [Part::Cylinder] Cylinder013  label="X-Achse005"
  Angle = 360
  AttacherType = Attacher::AttachEngine3D
  Height = 265
  Placement = pos=(42.5,115.4,2.5) rot=(1,0,0;1.5708rad)
  Radius = 4
FEATURE [App::DocumentObjectGroup] Group039  label="X"
  Group = -> [Cylinder012,Cylinder013,Box,Box011]
FEATURE [App::DocumentObjectGroup] Group036  label="Achsen-Drucker"
  Group = -> [Group039,Group038]
FEATURE [App::DocumentObjectGroup] Group032  label="Achsen"
  Group = -> [Group036,Group037]
FEATURE [PartDesign::FeatureBase] Clone013  label="P_Carrier_Part2"
  BaseFeature = -> Clone003
  Placement = pos=(1,-14,0) rot=(1,0,0;1.5708rad)
FEATURE [PartDesign::FeatureBase] Clone014  label="P_Carrier_Part1"
  BaseFeature = -> Clone004
  Placement = pos=(41,0,0) rot=(0,1,0;1.5708rad)
FEATURE [PartDesign::FeatureBase] Clone015  label="P_FanShroud"
  BaseFeature = -> Clone007
  Placement = pos=(-47,-5,-13) rot=(1,0,0;1.5708rad)
FEATURE [App::DocumentObjectGroup] Group002  label="Printables"
  Group = -> [Clone014,Clone013,Clone015]
FEATURE [Part::Feature] Fillet015001  label="FD1_Mainbody"
  Placement = pos=(-3,10,5) rot=(0,0,1;0rad)
  shape: bbox 29.02 x 55.27 x 72.13 mm, 158 faces (baked)
FEATURE [Part::Feature] Pocket042027001  label="FD1_Auslass"
  Placement = pos=(-3,10,5) rot=(0,0,1;0rad)
  shape: bbox 17.16 x 33 x 15.8 mm, 44 faces (baked)
FEATURE [Mesh::Feature] _0mm_Blower_Fan_v1_1  label="50mm_Blower_Fan_v1.1"
  Placement = pos=(-42,15,42.5) rot=(-0.707107,0,-0.707107;3.14159rad)
FEATURE [App::DocumentObjectGroup] Group030  label="Illustration"
  Group = -> [Box007,Clone008,Clone009,Clone010,Clone011,Clone012,Group028,Group032,_0mm_Blower_Fan_v1_1]
FEATURE [App::DocumentObjectGroup] Group001  label="Assembly"
  Group = -> [Clone003,Clone004,Clone006,Clone007,Group030,Fillet015001,Pocket042027001]
